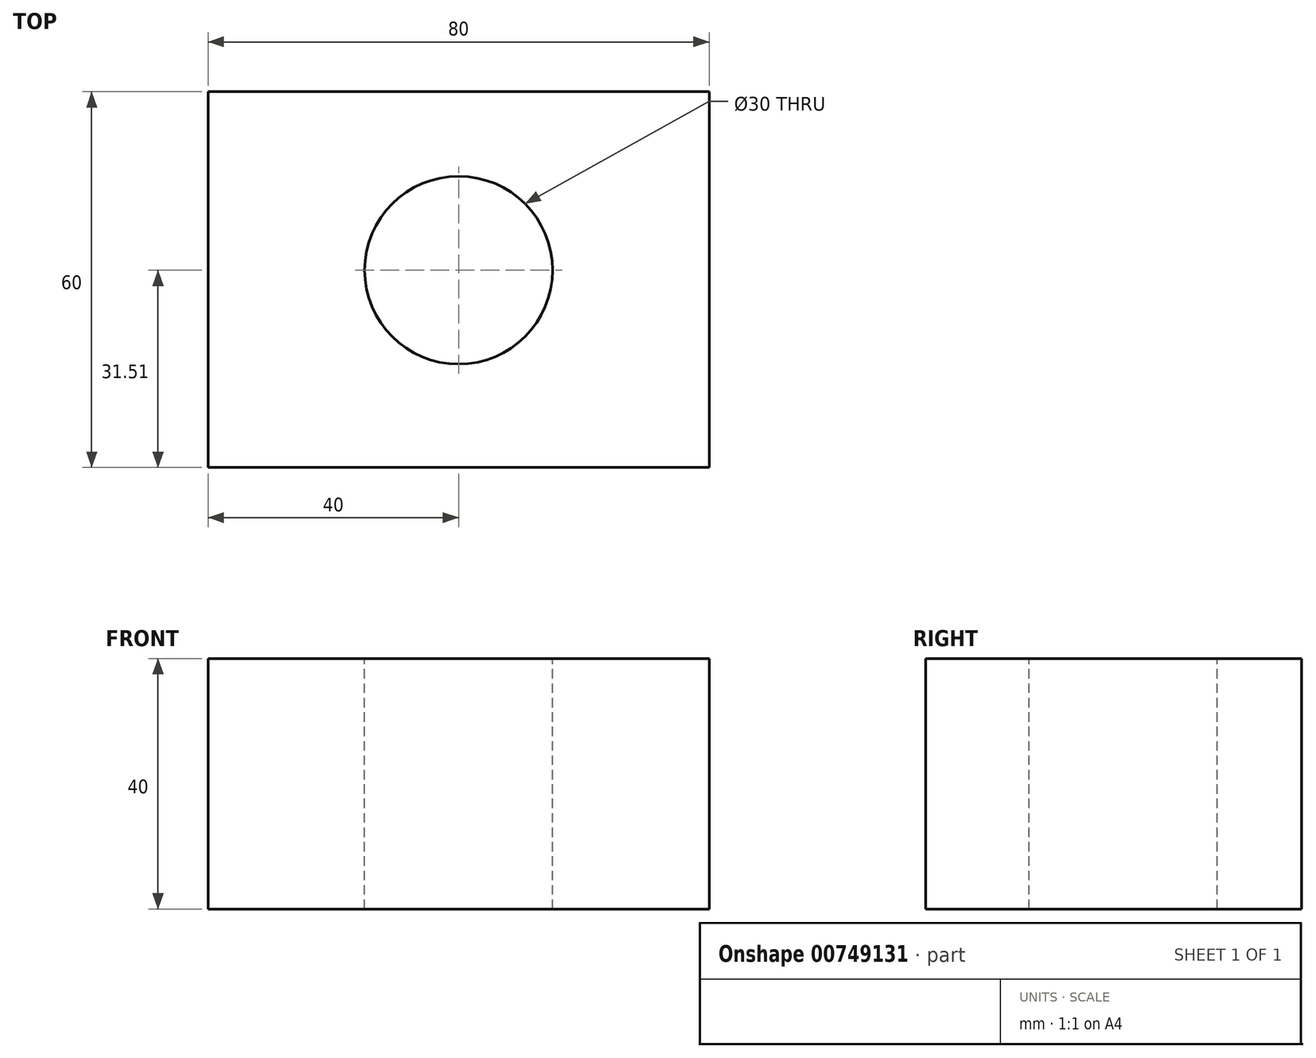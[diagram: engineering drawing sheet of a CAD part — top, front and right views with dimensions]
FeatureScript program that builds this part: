
annotation { "Feature Type Name" : "Feature", "Feature Type Description" : "" }
export const myFeature = defineFeature(function(context is Context, id is Id, definition is map)
    precondition{}
    {
        {
            var Q0;
            Q0=qCreatedBy(makeId("Front.planeOp"),FACE);
            var sketch = newSketch(context, id + "F0", { "sketchPlane" : qUnion([Q0])});
            skLineSegment(sketch, "E0.bottom", {"start": v(-40, -20) * mm, "end": v(40, -20) * mm});
            skLineSegment(sketch, "E0.top", {"start": v(-40, 20) * mm, "end": v(40, 20) * mm});
            skLineSegment(sketch, "E0.left", {"start": v(-40, -20) * mm, "end": v(-40, 20) * mm});
            skLineSegment(sketch, "E0.right", {"start": v(40, -20) * mm, "end": v(40, 20) * mm});
            skPoint(sketch, "E0.middle", {"position": v(0, 0) * mm});
            skSolve(sketch);
        }
        {
            var Q0;
            Q0=makeQuery(id+"F0.imprint","IMPRINT",FACE,{"disambiguationData":[TD([[makeQuery(id+"F0.imprint","IMPRINT",EDGE,{"derivedFrom":sQuery(id+"F0.wireOp",EDGE,"E0.bottom")}),1.0]])]});
            extrude(context, id + "F1", {"entities" : qUnion([Q0]), "depth" : 60 * mm, "offsetDistance" : 25 * mm});
        }
        {
            var Q0;
            Q0=makeQuery(id+"F1.opExtrude","SWEPT_FACE",FACE,{"disambiguationData":[OSD([sQuery(id+"F0.wireOp",EDGE,"E0.top")])]});
            var sketch = newSketch(context, id + "F2", { "sketchPlane" : qUnion([Q0])});
            skCircle(sketch, "E1", {"center": v(0, -28.5) * mm, "radius": 15 * mm});
            skSolve(sketch);
        }
        {
            var Q0;
            Q0=makeQuery(id+"F2.imprint","IMPRINT",FACE,{"disambiguationData":[TD([[makeQuery(id+"F2.imprint","IMPRINT",EDGE,{"derivedFrom":sQuery(id+"F2.wireOp",EDGE,"E1")}),1.0]])]});
            extrude(context, id + "F3", {"entities" : qUnion([Q0]), "operationType" : NewBodyOperationType.REMOVE, "endBound" : BoundingType.THROUGH_ALL, "oppositeDirection" : true, "depth" : 25 * mm, "offsetDistance" : 25 * mm});
        }
    });
